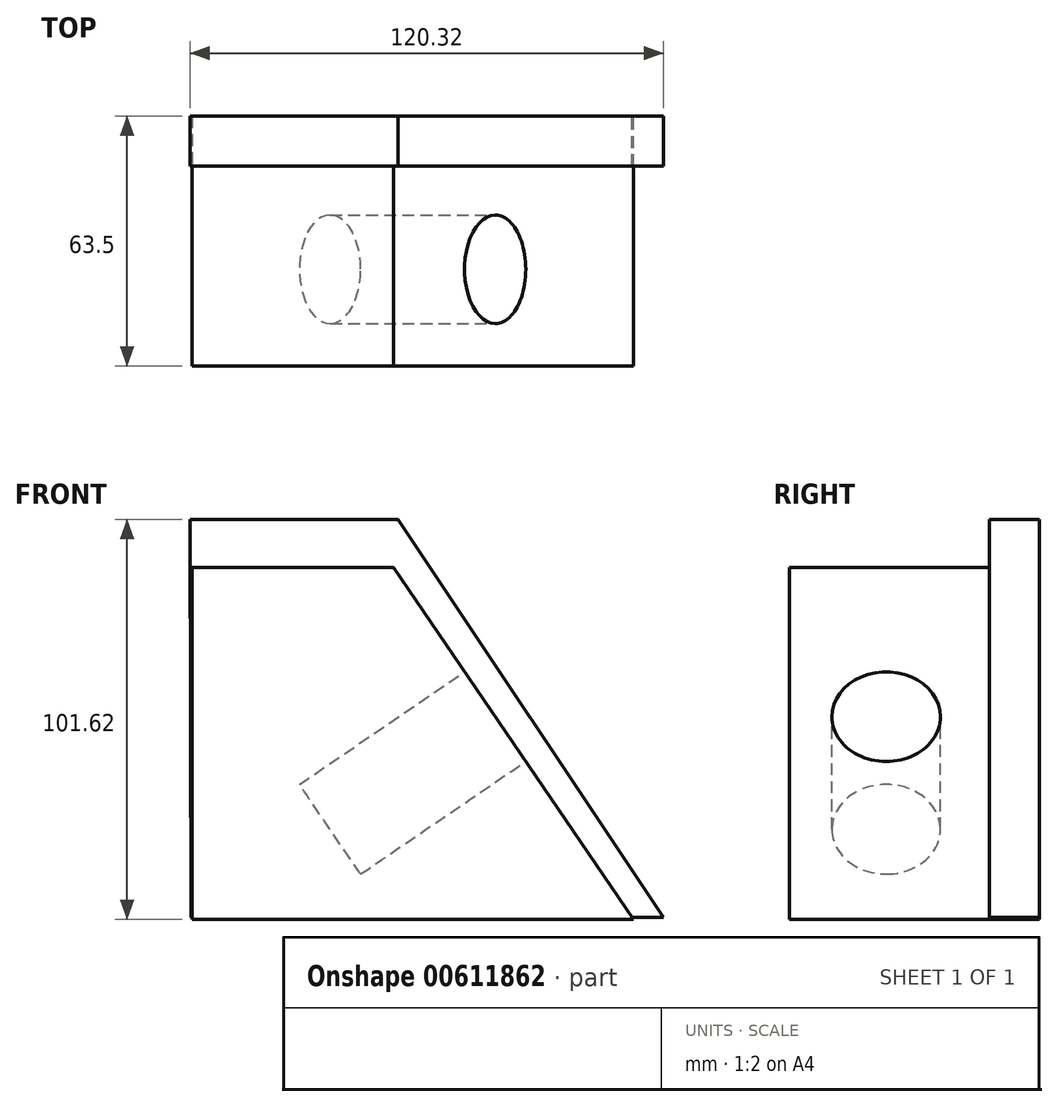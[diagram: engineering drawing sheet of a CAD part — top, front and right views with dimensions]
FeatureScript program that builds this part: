
annotation { "Feature Type Name" : "Feature", "Feature Type Description" : "" }
export const myFeature = defineFeature(function(context is Context, id is Id, definition is map)
    precondition{}
    {
        {
            var Q0;
            Q0=qCreatedBy(makeId("Front.planeOp"),FACE);
            var sketch = newSketch(context, id + "F0", { "sketchPlane" : qUnion([Q0])});
            skLineSegment(sketch, "E0", {"start": v(-44.82, 37.76) * mm, "end": v(-44.82, -51.7) * mm});
            skLineSegment(sketch, "E1", {"start": v(-44.82, -51.7) * mm, "end": v(67.36, -51.7) * mm});
            skLineSegment(sketch, "E2", {"start": v(67.36, -51.7) * mm, "end": v(6.32, 37.76) * mm});
            skLineSegment(sketch, "E3", {"start": v(6.32, 37.76) * mm, "end": v(-44.82, 37.76) * mm});
            skSolve(sketch);
        }
        {
            var Q0;
            Q0=makeQuery(id+"F0.imprint","IMPRINT",FACE,{"disambiguationData":[TD([[makeQuery(id+"F0.imprint","IMPRINT",EDGE,{"derivedFrom":sQuery(id+"F0.wireOp",EDGE,"E0")}),1.0]])]});
            extrude(context, id + "F1", {"entities" : qUnion([Q0]), "depth" : 63.5 * mm, "offsetDistance" : 25.4 * mm});
        }
        {
            var Q0;
            Q0=qCreatedBy(makeId("Front.planeOp"),FACE);
            var sketch = newSketch(context, id + "F2", { "sketchPlane" : qUnion([Q0])});
            skLineSegment(sketch, "E4", {"start": v(-45.04, -51.15) * mm, "end": v(74.97, -51.15) * mm});
            skLineSegment(sketch, "E5", {"start": v(74.97, -51.15) * mm, "end": v(7.48, 49.93) * mm});
            skLineSegment(sketch, "E6", {"start": v(7.48, 49.93) * mm, "end": v(-45.35, 49.93) * mm});
            skLineSegment(sketch, "E7", {"start": v(-45.35, 49.93) * mm, "end": v(-45.04, -51.15) * mm});
            skSolve(sketch);
        }
        {
            var Q0;
            Q0=makeQuery(id+"F2.imprint","IMPRINT",FACE,{"disambiguationData":[TD([[makeQuery(id+"F2.imprint","IMPRINT",EDGE,{"derivedFrom":sQuery(id+"F2.wireOp",EDGE,"E4")}),1.0]])]});
            extrude(context, id + "F3", {"entities" : qUnion([Q0]), "operationType" : NewBodyOperationType.ADD, "depth" : 12.7 * mm, "offsetDistance" : 25.4 * mm});
        }
        {
            var Q0;
            Q0=makeQuery(id+"F1.opExtrude","SWEPT_FACE",FACE,{"disambiguationData":[OSD([sQuery(id+"F0.wireOp",EDGE,"E2")])]});
            var sketch = newSketch(context, id + "F4", { "sketchPlane" : qUnion([Q0])});
            skCircle(sketch, "E8", {"center": v(-38.94, -18.27) * mm, "radius": 13.78 * mm});
            skSolve(sketch);
        }
        {
            var Q0;
            Q0=makeQuery(id+"F4.imprint","IMPRINT",FACE,{"disambiguationData":[TD([[makeQuery(id+"F4.imprint","IMPRINT",EDGE,{"derivedFrom":sQuery(id+"F4.wireOp",EDGE,"E8")}),1.0]])]});
            extrude(context, id + "F5", {"entities" : qUnion([Q0]), "operationType" : NewBodyOperationType.REMOVE, "oppositeDirection" : true, "depth" : 50.8 * mm, "offsetDistance" : 25.4 * mm});
        }
    });
